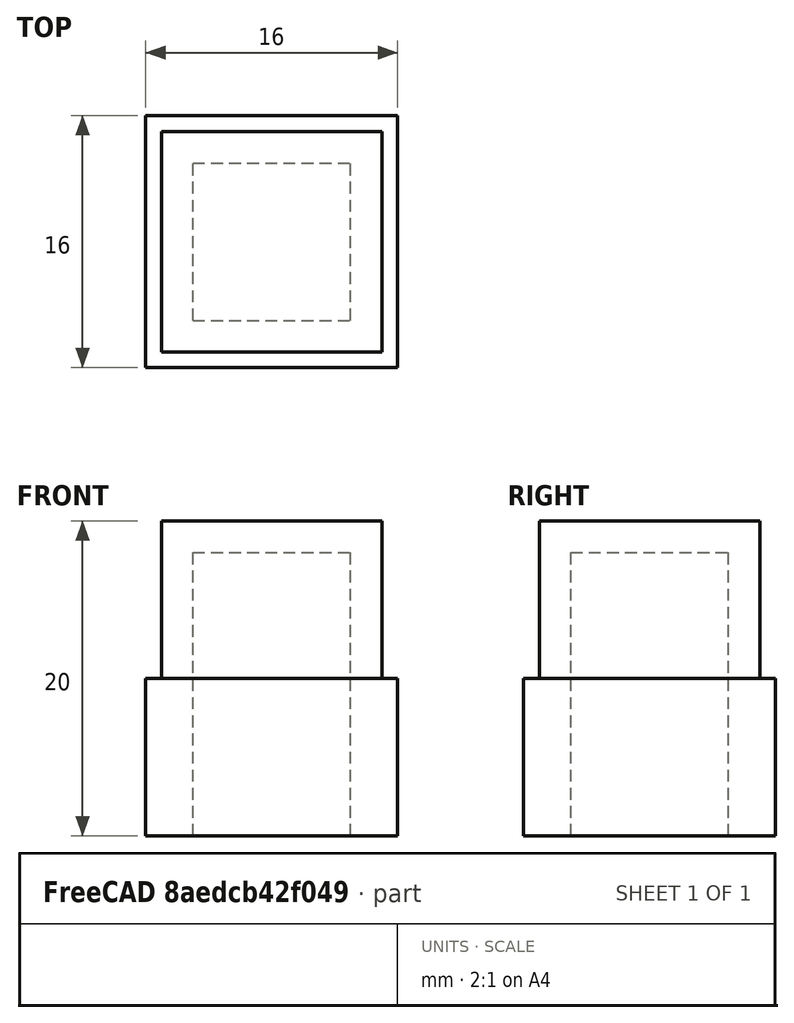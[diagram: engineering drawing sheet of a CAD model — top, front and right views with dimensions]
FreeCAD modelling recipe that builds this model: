
FCSTD DOCUMENT  (FreeCAD 0.18.3R)
Label: flat_slab
License: All rights reserved
LicenseURL: http://en.wikipedia.org/wiki/All_rights_reserved
objects: Part::Box×3, Part::Fuse×1, Part::Cut×1
note: 5 computed .brp shape members not serialized (recipe doc carries the construction recipe); baked Part::Feature solids carry a one-line shape summary decoded from their .brp

FEATURE [Part::Box] Box  label="Cube"
  AttacherType = Attacher::AttachEngine3D
  Height = 10
  Length = 16
  Placement = pos=(-8,-8,0) rot=(0,0,1;0rad)
  Width = 16
FEATURE [Part::Box] Box001  label="Cube001"
  AttacherType = Attacher::AttachEngine3D
  Height = 10
  Length = 14
  Placement = pos=(-7,-7,10) rot=(0,0,1;0rad)
  Width = 14
FEATURE [Part::Fuse] Fusion
  Base = -> Box
  Tool = -> Box001
FEATURE [Part::Box] Box002  label="Cube002"
  AttacherType = Attacher::AttachEngine3D
  Height = 18
  Length = 10
  Placement = pos=(-5,-5,0) rot=(0,0,1;0rad)
  Width = 10
FEATURE [Part::Cut] Cut
  Base = -> Fusion
  Tool = -> Box002
